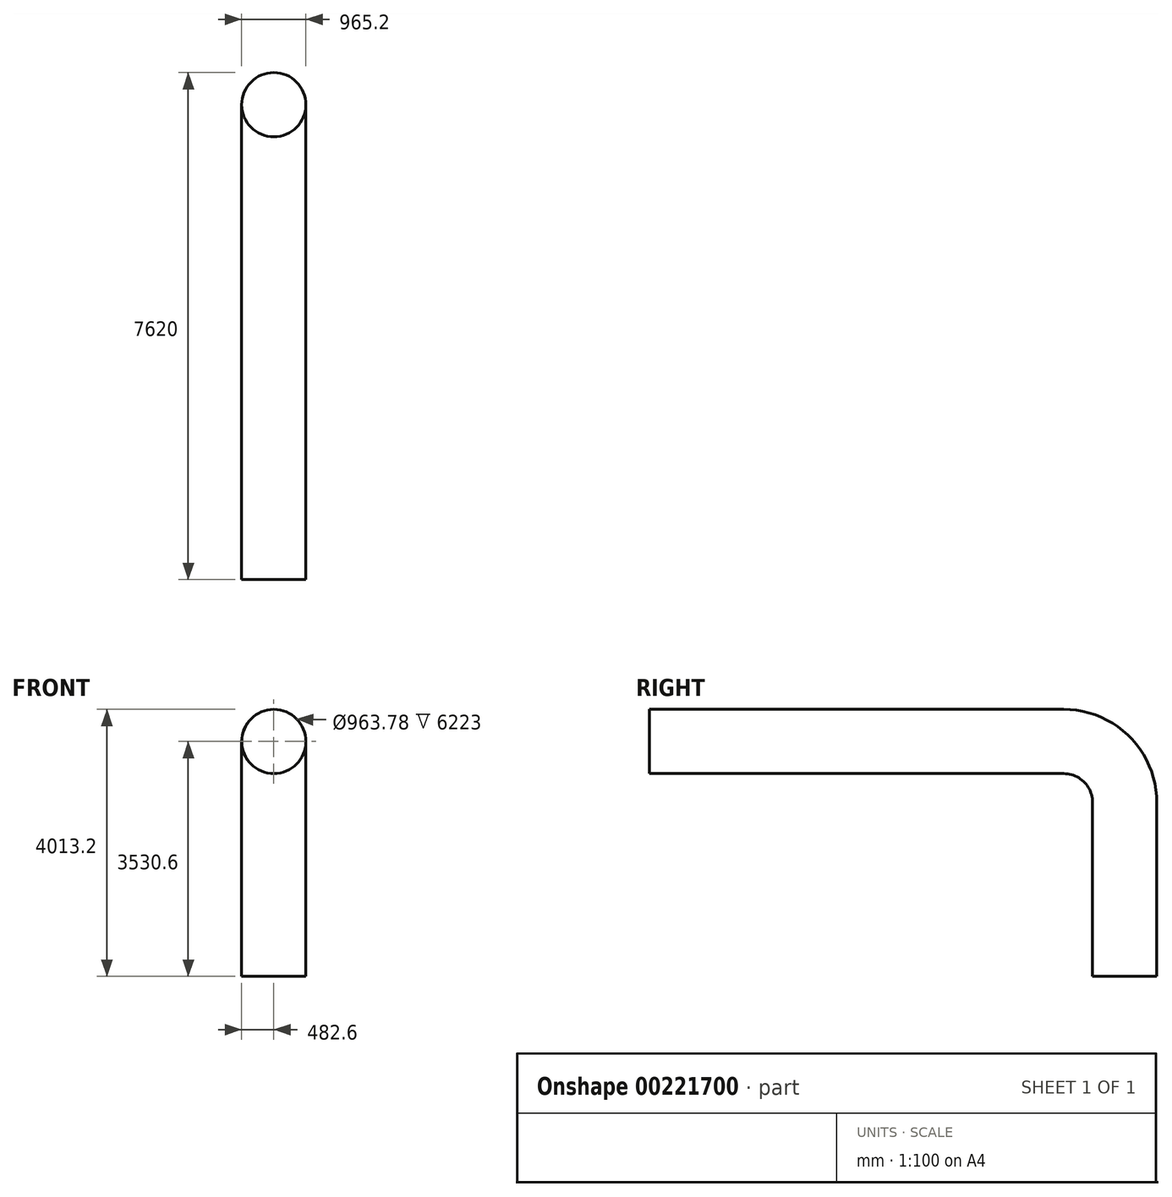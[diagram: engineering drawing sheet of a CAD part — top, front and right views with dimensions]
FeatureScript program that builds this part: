
annotation { "Feature Type Name" : "Feature", "Feature Type Description" : "" }
export const myFeature = defineFeature(function(context is Context, id is Id, definition is map)
    precondition{}
    {
        {
            var Q0;
            Q0=qCreatedBy(makeId("Front.planeOp"),FACE);
            var sketch = newSketch(context, id + "F0", { "sketchPlane" : qUnion([Q0])});
            skCircle(sketch, "E0", {"center": v(0, 0) * mm, "radius": 482.6 * mm});
            skCircle(sketch, "E1.0", {"center": v(0, 0) * mm, "radius": 481.89 * mm});
            skSolve(sketch);
        }
        {
            var Q0;
            Q0=qCreatedBy(makeId("Right.planeOp"),FACE);
            var sketch = newSketch(context, id + "F1", { "sketchPlane" : qUnion([Q0])});
            skLineSegment(sketch, "E2", {"start": v(0, 0) * mm, "end": v(6223, 0) * mm});
            skLineSegment(sketch, "E3", {"start": v(7137.4, -914.4) * mm, "end": v(7137.4, -3530.6) * mm});
            skPoint(sketch, "E4.visualSharp", {"position": v(7137.4, 0) * mm});
            skArc(sketch, "E4.filletArc", {"start": v(7137.4, -914.4) * mm, "mid": v(6869.58, -267.82) * mm, "end": v(6223, 0) * mm});
            skSolve(sketch);
        }
        {
            var Q0;
            Q0 = qSketchRegion(id + "F0", true);
            var Q1;
            Q1 = qConstructionFilter(qBodyType(qCreatedBy(id + "F1" ,EDGE), BodyType.WIRE), ConstructionObject.NO);
            sweep(context, id + "F2", {"profiles" : qUnion([Q0]), "path" : qUnion([Q1])});
        }
    });
